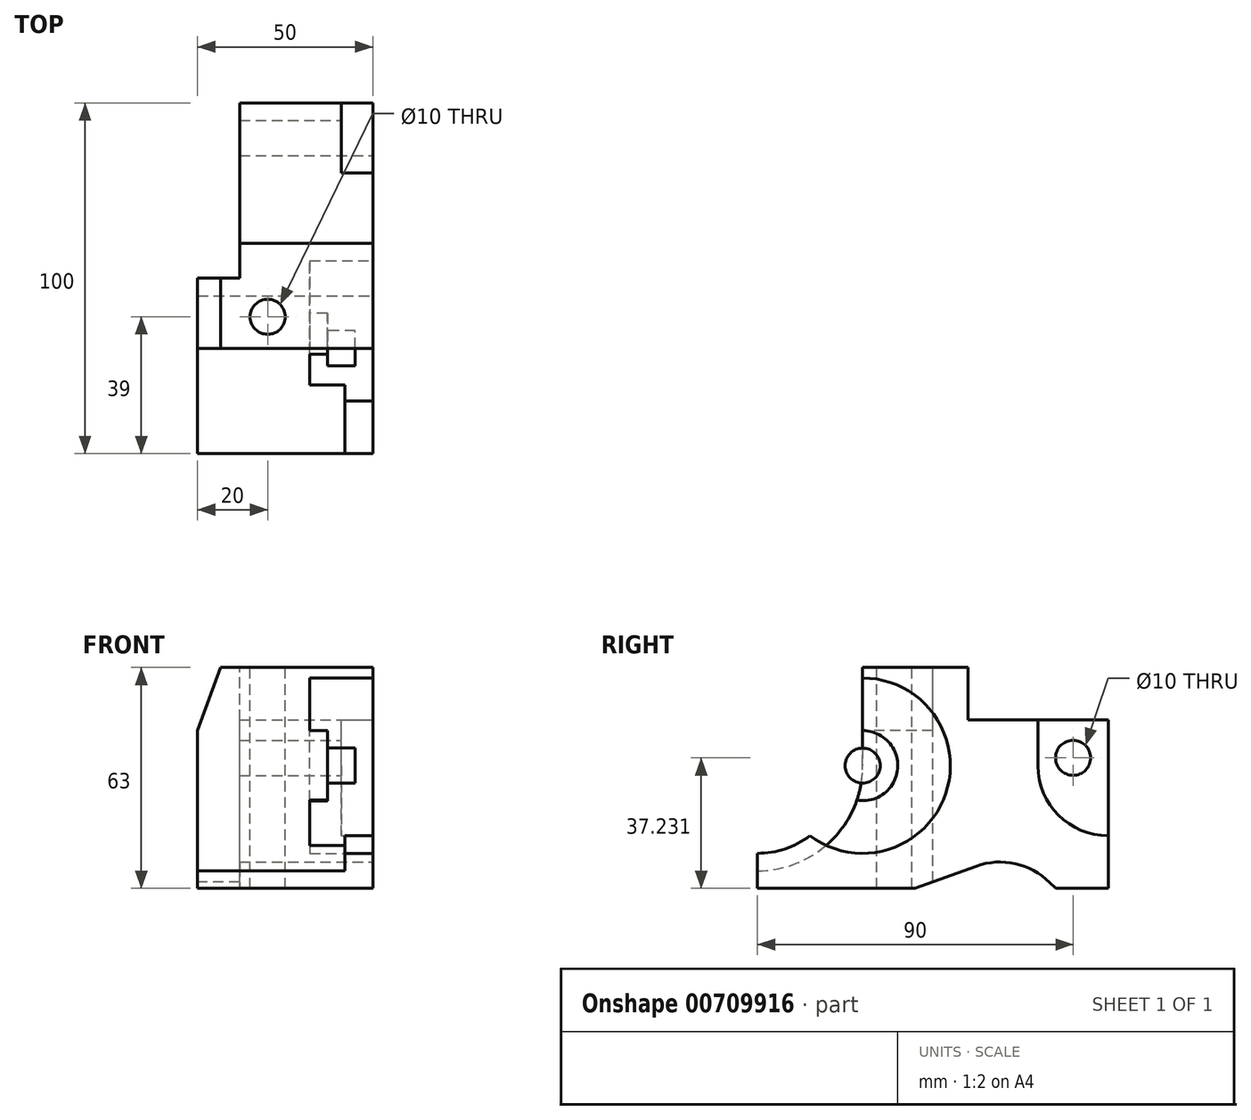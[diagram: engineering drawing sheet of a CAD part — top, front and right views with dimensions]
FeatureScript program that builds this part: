
annotation { "Feature Type Name" : "Feature", "Feature Type Description" : "" }
export const myFeature = defineFeature(function(context is Context, id is Id, definition is map)
    precondition{}
    {
        {
            var Q0;
            Q0=qCreatedBy(makeId("Right.planeOp"),FACE);
            var sketch = newSketch(context, id + "F0", { "sketchPlane" : qUnion([Q0])});
            skLineSegment(sketch, "E0", {"start": v(0, 0) * mm, "end": v(100, 0) * mm});
            skLineSegment(sketch, "E1", {"start": v(100, 0) * mm, "end": v(100, 63) * mm});
            skLineSegment(sketch, "E2", {"start": v(100, 63) * mm, "end": v(0, 63) * mm});
            skLineSegment(sketch, "E3", {"start": v(0, 63) * mm, "end": v(0, 0) * mm});
            skSolve(sketch);
        }
        {
            var Q0;
            Q0=makeQuery(id+"F0.imprint","IMPRINT",FACE,{"disambiguationData":[TD([[makeQuery(id+"F0.imprint","IMPRINT",EDGE,{"derivedFrom":sQuery(id+"F0.wireOp",EDGE,"E0")}),1.0]])]});
            extrude(context, id + "F1", {"entities" : qUnion([Q0]), "depth" : 50 * mm, "offsetDistance" : 25 * mm});
        }
        {
            var Q0;
            Q0=makeQuery(id+"F1.opExtrude","CAP_FACE",FACE,{"disambiguationData":[OSD([sQuery(id+"F0.wireOp",EDGE,"E0"),sQuery(id+"F0.wireOp",EDGE,"E1"),sQuery(id+"F0.wireOp",EDGE,"E2"),sQuery(id+"F0.wireOp",EDGE,"E3")])],"isStart":false});
            var sketch = newSketch(context, id + "F2", { "sketchPlane" : qUnion([Q0])});
            skLineSegment(sketch, "E4", {"start": v(45, 0) * mm, "end": v(62.35, 6.32) * mm});
            skLineSegment(sketch, "E5", {"start": v(85, 0) * mm, "end": v(83.34, 1.66) * mm});
            skArc(sketch, "E6", {"start": v(62.35, 6.32) * mm, "mid": v(73.52, 7.05) * mm, "end": v(83.34, 1.66) * mm});
            skLineSegment(sketch, "E7", {"start": v(45, 0) * mm, "end": v(85, 0) * mm});
            skSolve(sketch);
        }
        {
            var Q0;
            Q0=makeQuery(id+"F2.imprint","IMPRINT",FACE,{"disambiguationData":[TD([[makeQuery(id+"F2.imprint","IMPRINT",EDGE,{"derivedFrom":sQuery(id+"F2.wireOp",EDGE,"E4")}),-1.0]])]});
            extrude(context, id + "F3", {"entities" : qUnion([Q0]), "operationType" : NewBodyOperationType.REMOVE, "endBound" : BoundingType.THROUGH_ALL, "oppositeDirection" : true, "depth" : 25 * mm, "offsetDistance" : 25 * mm});
        }
        {
            var Q0;
            Q0=makeQuery(id+"F1.opExtrude","CAP_FACE",FACE,{"disambiguationData":[OSD([sQuery(id+"F0.wireOp",EDGE,"E0"),sQuery(id+"F0.wireOp",EDGE,"E1"),sQuery(id+"F0.wireOp",EDGE,"E2"),sQuery(id+"F0.wireOp",EDGE,"E3")])],"isStart":false});
            var sketch = newSketch(context, id + "F4", { "sketchPlane" : qUnion([Q0])});
            skLineSegment(sketch, "E8", {"start": v(60, 63) * mm, "end": v(60, 48) * mm});
            skLineSegment(sketch, "E9", {"start": v(60, 48) * mm, "end": v(100, 48) * mm});
            skLineSegment(sketch, "E10", {"start": v(100, 48) * mm, "end": v(100, 63) * mm});
            skLineSegment(sketch, "E11", {"start": v(100, 63) * mm, "end": v(60, 63) * mm});
            skSolve(sketch);
        }
        {
            var Q0;
            Q0=makeQuery(id+"F4.imprint","IMPRINT",FACE,{"disambiguationData":[TD([[makeQuery(id+"F4.imprint","IMPRINT",EDGE,{"derivedFrom":sQuery(id+"F4.wireOp",EDGE,"E8")}),1.0]])]});
            extrude(context, id + "F5", {"entities" : qUnion([Q0]), "operationType" : NewBodyOperationType.REMOVE, "endBound" : BoundingType.THROUGH_ALL, "oppositeDirection" : true, "depth" : 25 * mm, "offsetDistance" : 25 * mm});
        }
        {
            var Q0;
            Q0=makeQuery(id+"F1.opExtrude","CAP_FACE",FACE,{"disambiguationData":[OSD([sQuery(id+"F0.wireOp",EDGE,"E0"),sQuery(id+"F0.wireOp",EDGE,"E1"),sQuery(id+"F0.wireOp",EDGE,"E2"),sQuery(id+"F0.wireOp",EDGE,"E3")])],"isStart":false});
            var sketch = newSketch(context, id + "F6", { "sketchPlane" : qUnion([Q0])});
            skCircle(sketch, "E12", {"center": v(100, 35) * mm, "radius": 20 * mm});
            skLineSegment(sketch, "E13", {"start": v(80, 35) * mm, "end": v(80, 48) * mm});
            skLineSegment(sketch, "E14", {"start": v(80, 48) * mm, "end": v(100, 48) * mm});
            skLineSegment(sketch, "E15", {"start": v(100, 48) * mm, "end": v(100, 15) * mm});
            skSolve(sketch);
        }
        {
            var Q0;
            {var subQ4=sQuery(id+"F6.wireOp",EDGE,"E15");Q0=makeQuery(id+"F6.imprint","IMPRINT",FACE,{"disambiguationData":[TD([[makeQuery(id+"F6.imprint","IMPRINT",EDGE,{"derivedFrom":subQ4}),1.0]])]});}
            var Q1;
            {var subQ0=sQuery(id+"F6.wireOp",EDGE,"E13");Q1=makeQuery(id+"F6.imprint","IMPRINT",FACE,{"disambiguationData":[TD([[makeQuery(id+"F6.imprint","IMPRINT",EDGE,{"derivedFrom":subQ0}),-1.0]])]});}
            extrude(context, id + "F7", {"entities" : qUnion([Q0, Q1]), "operationType" : NewBodyOperationType.REMOVE, "oppositeDirection" : true, "depth" : 9 * mm, "offsetDistance" : 25 * mm});
        }
        {
            var Q0;
            Q0=makeQuery(id+"F7.boolean.opBoolean","COPY",FACE,{"derivedFrom":makeQuery(id+"F7.opExtrude","CAP_FACE",FACE,{"disambiguationData":[OSD([sQuery(id+"F6.wireOp",EDGE,"E12"),sQuery(id+"F6.wireOp",EDGE,"E13"),sQuery(id+"F6.wireOp",EDGE,"E14"),sQuery(id+"F6.wireOp",EDGE,"E15")])],"isStart":false})});
            var sketch = newSketch(context, id + "F8", { "sketchPlane" : qUnion([Q0])});
            skCircle(sketch, "E16", {"center": v(90, 37.23) * mm, "radius": 5 * mm});
            skSolve(sketch);
        }
        {
            var Q0;
            Q0=makeQuery(id+"F8.imprint","IMPRINT",FACE,{"disambiguationData":[TD([[makeQuery(id+"F8.imprint","IMPRINT",EDGE,{"derivedFrom":sQuery(id+"F8.wireOp",EDGE,"E16")}),1.0]])]});
            extrude(context, id + "F9", {"entities" : qUnion([Q0]), "operationType" : NewBodyOperationType.REMOVE, "endBound" : BoundingType.THROUGH_ALL, "oppositeDirection" : true, "depth" : 25 * mm, "offsetDistance" : 25 * mm});
        }
        {
            var Q0;
            Q0=makeQuery(id+"F1.opExtrude","SWEPT_FACE",FACE,{"disambiguationData":[OSD([sQuery(id+"F0.wireOp",EDGE,"E2")])]});
            var sketch = newSketch(context, id + "F10", { "sketchPlane" : qUnion([Q0])});
            skLineSegment(sketch, "E17", {"start": v(0, 50) * mm, "end": v(12, 50) * mm});
            skLineSegment(sketch, "E18", {"start": v(12, 50) * mm, "end": v(12, 100) * mm});
            skLineSegment(sketch, "E19", {"start": v(12, 100) * mm, "end": v(0, 100) * mm});
            skLineSegment(sketch, "E20", {"start": v(0, 100) * mm, "end": v(0, 50) * mm});
            skSolve(sketch);
        }
        {
            var Q0;
            {var subQ0=sQuery(id+"F10.wireOp",EDGE,"E17");Q0=makeQuery(id+"F10.imprint","IMPRINT",FACE,{"disambiguationData":[TD([[makeQuery(id+"F10.imprint","IMPRINT",EDGE,{"derivedFrom":subQ0}),1.0]])]});}
            var Q1;
            {var subQ0=sQuery(id+"F10.wireOp",EDGE,"E19");Q1=makeQuery(id+"F10.imprint","IMPRINT",FACE,{"disambiguationData":[TD([[makeQuery(id+"F10.imprint","IMPRINT",EDGE,{"derivedFrom":subQ0}),1.0]])]});}
            extrude(context, id + "F11", {"entities" : qUnion([Q0, Q1]), "operationType" : NewBodyOperationType.REMOVE, "endBound" : BoundingType.THROUGH_ALL, "oppositeDirection" : true, "depth" : 25 * mm, "offsetDistance" : 25 * mm});
        }
        {
            var Q0;
            Q0=makeQuery(id+"F1.opExtrude","SWEPT_FACE",FACE,{"disambiguationData":[OSD([sQuery(id+"F0.wireOp",EDGE,"E3")])]});
            var sketch = newSketch(context, id + "F12", { "sketchPlane" : qUnion([Q0])});
            skLineSegment(sketch, "E21", {"start": v(0, 45) * mm, "end": v(6.55, 63) * mm});
            skLineSegment(sketch, "E22", {"start": v(6.55, 63) * mm, "end": v(0, 63) * mm});
            skLineSegment(sketch, "E23", {"start": v(0, 63) * mm, "end": v(0, 45) * mm});
            skSolve(sketch);
        }
        {
            var Q0;
            Q0=makeQuery(id+"F12.imprint","IMPRINT",FACE,{"disambiguationData":[TD([[makeQuery(id+"F12.imprint","IMPRINT",EDGE,{"derivedFrom":sQuery(id+"F12.wireOp",EDGE,"E21")}),1.0]])]});
            extrude(context, id + "F13", {"entities" : qUnion([Q0]), "operationType" : NewBodyOperationType.REMOVE, "endBound" : BoundingType.THROUGH_ALL, "depth" : 25 * mm, "offsetDistance" : 25 * mm});
        }
        {
            var Q0;
            Q0=makeQuery(id+"F1.opExtrude","SWEPT_FACE",FACE,{"disambiguationData":[OSD([sQuery(id+"F0.wireOp",EDGE,"E3")])]});
            var sketch = newSketch(context, id + "F14", { "sketchPlane" : qUnion([Q0])});
            skLineSegment(sketch, "E24", {"start": v(0, 45) * mm, "end": v(6.55, 63) * mm});
            skLineSegment(sketch, "E25", {"start": v(6.55, 63) * mm, "end": v(0, 63) * mm});
            skLineSegment(sketch, "E26", {"start": v(0, 63) * mm, "end": v(0, 45) * mm});
            skSolve(sketch);
        }
        {
            var Q0;
            Q0 = qSketchRegion(id + "F14", true);
            extrude(context, id + "F15", {"entities" : qUnion([Q0]), "operationType" : NewBodyOperationType.REMOVE, "endBound" : BoundingType.THROUGH_ALL, "oppositeDirection" : true, "depth" : 25 * mm, "offsetDistance" : 25 * mm});
        }
        {
            var Q0;
            Q0=makeQuery(id+"F1.opExtrude","CAP_FACE",FACE,{"disambiguationData":[OSD([sQuery(id+"F0.wireOp",EDGE,"E0"),sQuery(id+"F0.wireOp",EDGE,"E1"),sQuery(id+"F0.wireOp",EDGE,"E2"),sQuery(id+"F0.wireOp",EDGE,"E3")])],"isStart":false});
            var sketch = newSketch(context, id + "F16", { "sketchPlane" : qUnion([Q0])});
            skCircle(sketch, "E27", {"center": v(30, 35) * mm, "radius": 25 * mm});
            skSolve(sketch);
        }
        {
            var Q0;
            Q0=makeQuery(id+"F16.imprint","IMPRINT",FACE,{"disambiguationData":[TD([[makeQuery(id+"F16.imprint","IMPRINT",EDGE,{"derivedFrom":sQuery(id+"F16.wireOp",EDGE,"E27")}),1.0]])]});
            extrude(context, id + "F17", {"entities" : qUnion([Q0]), "operationType" : NewBodyOperationType.REMOVE, "oppositeDirection" : true, "depth" : 18 * mm, "offsetDistance" : 25 * mm});
        }
        {
            var Q0;
            Q0=makeQuery(id+"F17.boolean.opBoolean","COPY",FACE,{"derivedFrom":makeQuery(id+"F17.opExtrude","CAP_FACE",FACE,{"disambiguationData":[OSD([sQuery(id+"F16.wireOp",EDGE,"E27")])],"isStart":false})});
            var sketch = newSketch(context, id + "F18", { "sketchPlane" : qUnion([Q0])});
            skCircle(sketch, "E28", {"center": v(30, 35) * mm, "radius": 10 * mm});
            skSolve(sketch);
        }
        {
            var Q0;
            Q0=makeQuery(id+"F18.imprint","IMPRINT",FACE,{"disambiguationData":[TD([[makeQuery(id+"F18.imprint","IMPRINT",EDGE,{"derivedFrom":sQuery(id+"F18.wireOp",EDGE,"E28")}),1.0]])]});
            extrude(context, id + "F19", {"entities" : qUnion([Q0]), "operationType" : NewBodyOperationType.ADD, "depth" : 5 * mm, "offsetDistance" : 25 * mm});
        }
        {
            var Q0;
            Q0=makeQuery(id+"F1.opExtrude","CAP_FACE",FACE,{"disambiguationData":[OSD([sQuery(id+"F0.wireOp",EDGE,"E0"),sQuery(id+"F0.wireOp",EDGE,"E1"),sQuery(id+"F0.wireOp",EDGE,"E2"),sQuery(id+"F0.wireOp",EDGE,"E3")])],"isStart":false});
            var sketch = newSketch(context, id + "F20", { "sketchPlane" : qUnion([Q0])});
            skCircle(sketch, "E29", {"center": v(0, 35) * mm, "radius": 25 * mm});
            skSolve(sketch);
        }
        {
            var Q0;
            Q0=makeQuery(id+"F1.opExtrude","CAP_FACE",FACE,{"disambiguationData":[OSD([sQuery(id+"F0.wireOp",EDGE,"E0"),sQuery(id+"F0.wireOp",EDGE,"E1"),sQuery(id+"F0.wireOp",EDGE,"E2"),sQuery(id+"F0.wireOp",EDGE,"E3")])],"isStart":true});
            var sketch = newSketch(context, id + "F21", { "sketchPlane" : qUnion([Q0])});
            skArc(sketch, "E30", {"start": v(-30, 35) * mm, "mid": v(21.93, 14.53) * mm, "end": v(-2.07, 64.93) * mm});
            skLineSegment(sketch, "E31", {"start": v(-30, 35) * mm, "end": v(-30, 63) * mm});
            skLineSegment(sketch, "E32", {"start": v(-30, 63) * mm, "end": v(0, 65.07) * mm});
            skSolve(sketch);
        }
        {
            var Q0;
            Q0 = qSketchRegion(id + "F21", true);
            extrude(context, id + "F22", {"entities" : qUnion([Q0]), "operationType" : NewBodyOperationType.REMOVE, "oppositeDirection" : true, "depth" : 42 * mm, "offsetDistance" : 25 * mm});
        }
        {
            var Q0;
            Q0 = qSketchRegion(id + "F20", true);
            extrude(context, id + "F23", {"entities" : qUnion([Q0]), "operationType" : NewBodyOperationType.REMOVE, "oppositeDirection" : true, "depth" : 8 * mm, "offsetDistance" : 25 * mm});
        }
        {
            var Q0;
            Q0=makeQuery(id+"F19.opExtrude","CAP_FACE",FACE,{"disambiguationData":[OSD([sQuery(id+"F18.wireOp",EDGE,"E28")])],"isStart":false});
            var sketch = newSketch(context, id + "F24", { "sketchPlane" : qUnion([Q0])});
            skCircle(sketch, "E33", {"center": v(30, 35) * mm, "radius": 5 * mm});
            skSolve(sketch);
        }
        {
            var Q0;
            {var subQ0=sQuery(id+"F24.wireOp",EDGE,"E33");var subQ1=makeQuery(id+"F19.opExtrude","CAP_FACE",FACE,{"disambiguationData":[OSD([sQuery(id+"F18.wireOp",EDGE,"E28")])],"isStart":false});var subQ2=makeQuery(id+"F22.boolean.opBoolean","INTERSECT",EDGE,{"derivedFrom":[subQ1,makeQuery(id+"F22.opExtrude","SWEPT_FACE",FACE,{"disambiguationData":[OSD([sQuery(id+"F21.wireOp",EDGE,"E30")])]})]});var subQ3=makeQuery(id+"F24.imprint","INTERSECT",VERTEX,{"derivedFrom":[subQ2,subQ0]});Q0=makeQuery(id+"F24.imprint","IMPRINT",FACE,{"disambiguationData":[TD([[makeQuery(id+"F24.imprint","IMPRINT",EDGE,{"disambiguationData":[TD([[subQ3,-1.0]])],"derivedFrom":subQ0}),1.0]])]});}
            var Q1;
            {var subQ0=sQuery(id+"F24.wireOp",EDGE,"E33");var subQ1=makeQuery(id+"F19.opExtrude","CAP_FACE",FACE,{"disambiguationData":[OSD([sQuery(id+"F18.wireOp",EDGE,"E28")])],"isStart":false});var subQ2=makeQuery(id+"F22.boolean.opBoolean","INTERSECT",EDGE,{"derivedFrom":[subQ1,makeQuery(id+"F22.opExtrude","SWEPT_FACE",FACE,{"disambiguationData":[OSD([sQuery(id+"F21.wireOp",EDGE,"E30")])]})]});var subQ3=makeQuery(id+"F24.imprint","INTERSECT",VERTEX,{"derivedFrom":[subQ2,subQ0]});Q1=makeQuery(id+"F24.imprint","IMPRINT",FACE,{"disambiguationData":[TD([[makeQuery(id+"F24.imprint","IMPRINT",EDGE,{"disambiguationData":[TD([[subQ3,1.0]])],"derivedFrom":subQ0}),1.0]])]});}
            extrude(context, id + "F25", {"entities" : qUnion([Q0, Q1]), "operationType" : NewBodyOperationType.ADD, "depth" : 8 * mm, "offsetDistance" : 25 * mm});
        }
        {
            var Q0;
            {var subQ0=sQuery(id+"F21.wireOp",EDGE,"E31");Q0=makeQuery(id+"F23.boolean.opBoolean","SPLIT",FACE,{"disambiguationData":[TD([makeQuery(id+"F1.opExtrude","SWEPT_FACE",FACE,{"disambiguationData":[OSD([sQuery(id+"F0.wireOp",EDGE,"E2")])]})])],"derivedFrom":makeQuery(id+"F22.boolean.opBoolean","COPY",FACE,{"derivedFrom":makeQuery(id+"F22.opExtrude","CAP_FACE",FACE,{"disambiguationData":[OSD([sQuery(id+"F21.wireOp",EDGE,"E30"),subQ0,sQuery(id+"F21.wireOp",EDGE,"E32")])],"isStart":false})})});}
            var sketch = newSketch(context, id + "F26", { "sketchPlane" : qUnion([Q0])});
            skLineSegment(sketch, "E34.bottom", {"start": v(-30, 63) * mm, "end": v(10, 63) * mm});
            skLineSegment(sketch, "E34.top", {"start": v(-30, 54) * mm, "end": v(10, 54) * mm});
            skLineSegment(sketch, "E34.left", {"start": v(-30, 63) * mm, "end": v(-30, 54) * mm});
            skLineSegment(sketch, "E34.right", {"start": v(10, 63) * mm, "end": v(10, 54) * mm});
            skSolve(sketch);
        }
        {
            var Q0;
            Q0 = qSketchRegion(id + "F26", true);
            extrude(context, id + "F27", {"entities" : qUnion([Q0]), "operationType" : NewBodyOperationType.REMOVE, "endBound" : BoundingType.THROUGH_ALL, "oppositeDirection" : true, "depth" : 25 * mm, "offsetDistance" : 25 * mm});
        }
        {
            var Q0;
            Q0=makeQuery(id+"F1.opExtrude","SWEPT_FACE",FACE,{"disambiguationData":[OSD([sQuery(id+"F0.wireOp",EDGE,"E2")])]});
            var sketch = newSketch(context, id + "F28", { "sketchPlane" : qUnion([Q0])});
            skCircle(sketch, "E35", {"center": v(20, 39) * mm, "radius": 5 * mm});
            skSolve(sketch);
        }
        {
            var Q0;
            Q0 = qSketchRegion(id + "F28", true);
            extrude(context, id + "F29", {"entities" : qUnion([Q0]), "operationType" : NewBodyOperationType.REMOVE, "endBound" : BoundingType.THROUGH_ALL, "oppositeDirection" : true, "depth" : 25 * mm, "offsetDistance" : 25 * mm});
        }
    });
